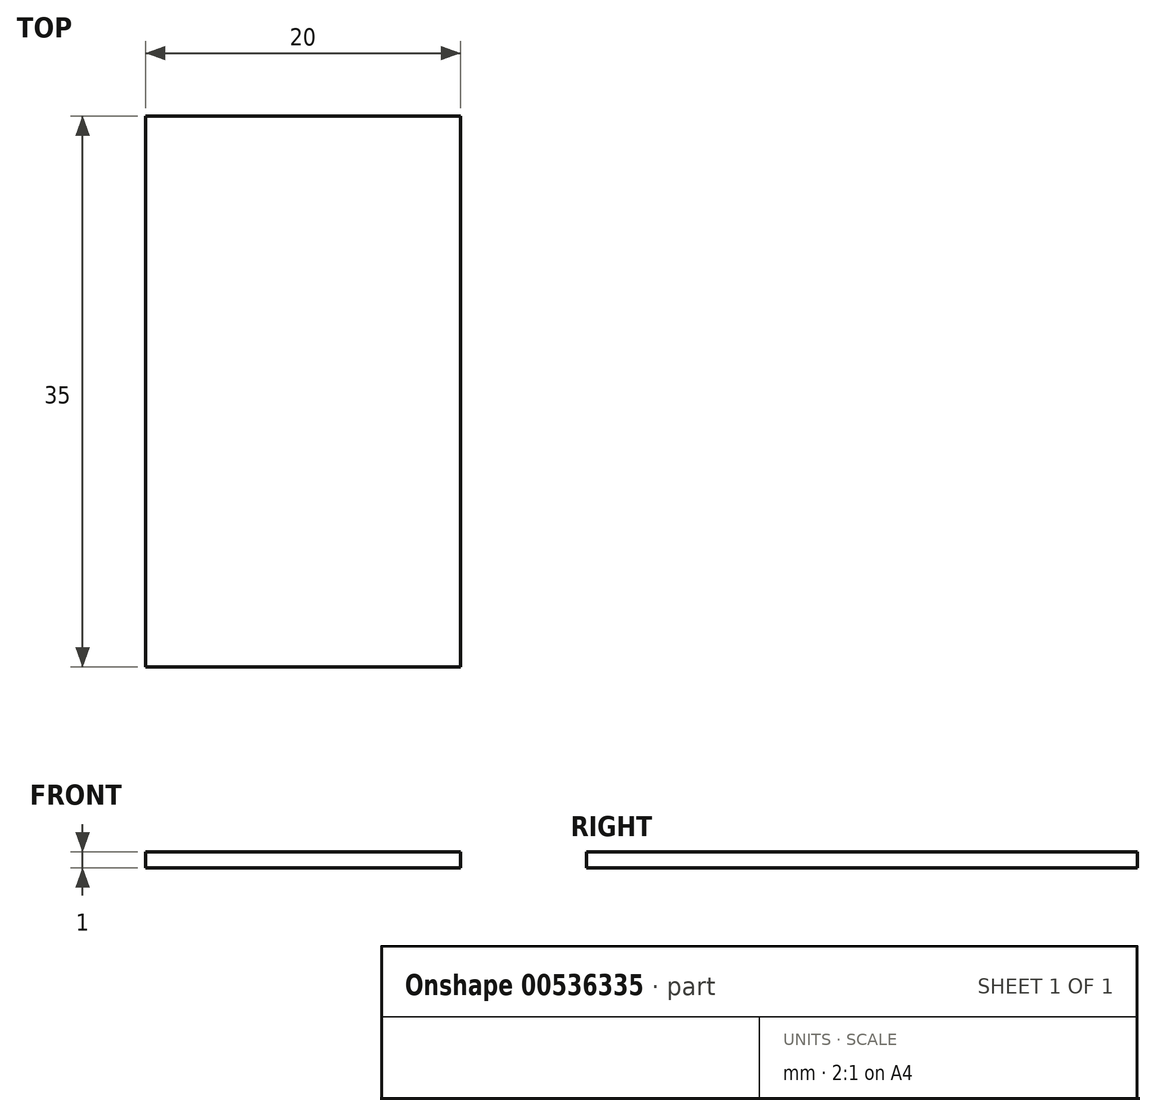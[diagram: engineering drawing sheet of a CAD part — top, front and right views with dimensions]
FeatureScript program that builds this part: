
annotation { "Feature Type Name" : "Feature", "Feature Type Description" : "" }
export const myFeature = defineFeature(function(context is Context, id is Id, definition is map)
    precondition{}
    {
        {
            var Q0;
            Q0=qCreatedBy(makeId("Top.planeOp"),FACE);
            var sketch = newSketch(context, id + "F0", { "sketchPlane" : qUnion([Q0])});
            skLineSegment(sketch, "E0.bottom", {"start": v(10, -17.5) * mm, "end": v(-10, -17.5) * mm});
            skLineSegment(sketch, "E0.top", {"start": v(10, 17.5) * mm, "end": v(-10, 17.5) * mm});
            skLineSegment(sketch, "E0.left", {"start": v(10, -17.5) * mm, "end": v(10, 17.5) * mm});
            skLineSegment(sketch, "E0.right", {"start": v(-10, -17.5) * mm, "end": v(-10, 17.5) * mm});
            skPoint(sketch, "E0.middle", {"position": v(0, 0) * mm});
            skSolve(sketch);
        }
        {
            var Q0;
            Q0=makeQuery(id+"F0.imprint","IMPRINT",FACE,{"disambiguationData":[TD([[makeQuery(id+"F0.imprint","IMPRINT",EDGE,{"derivedFrom":sQuery(id+"F0.wireOp",EDGE,"E0.bottom")}),-1.0]])]});
            extrude(context, id + "F1", {"entities" : qUnion([Q0]), "depth" : 1 * mm, "offsetDistance" : 25 * mm});
        }
    });
